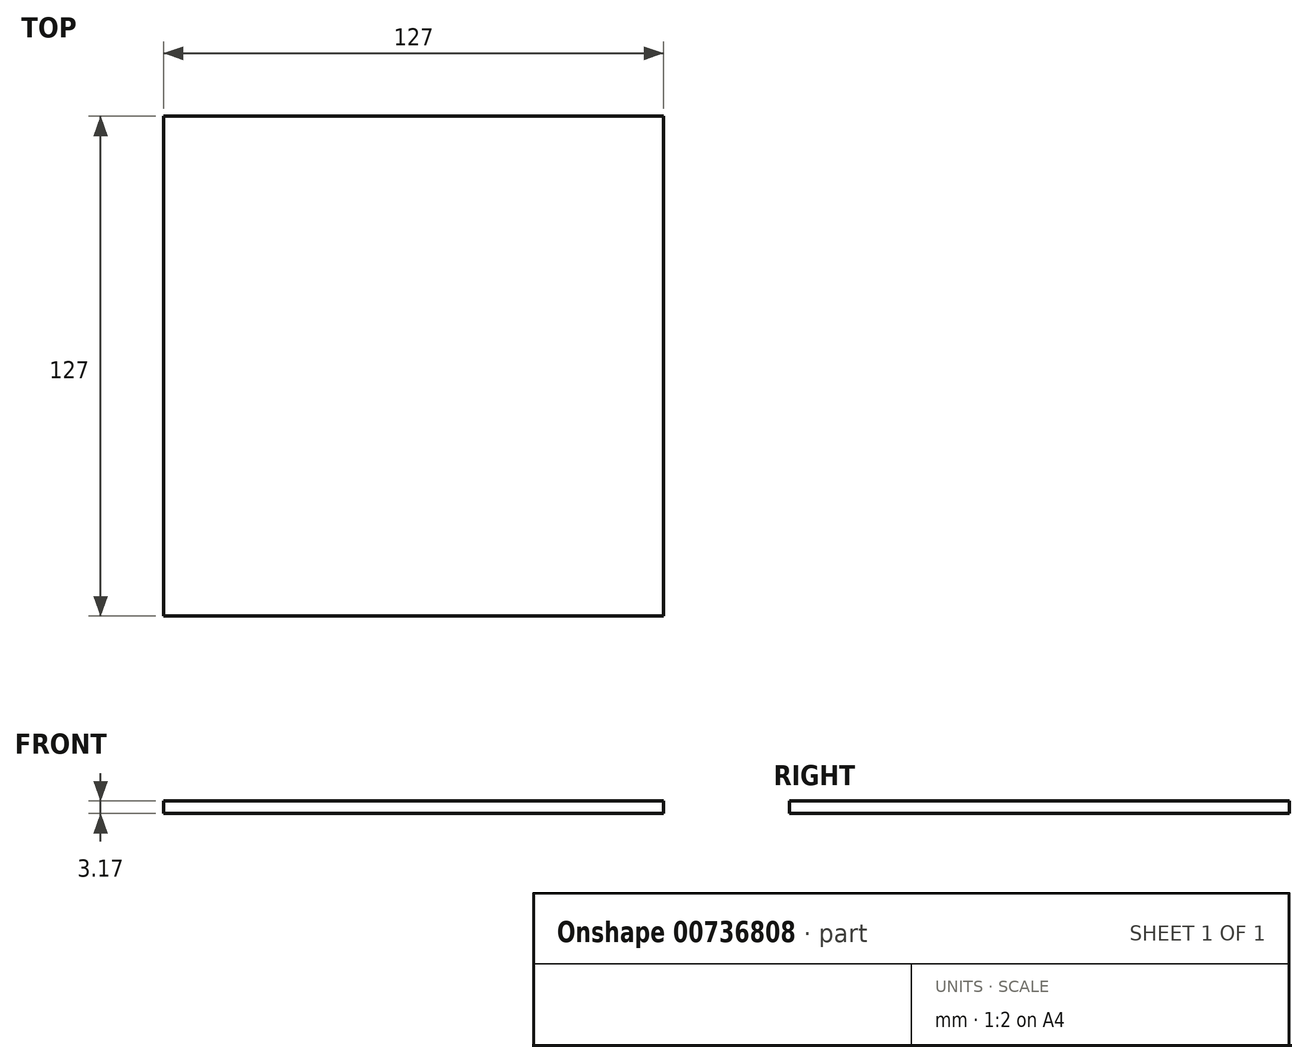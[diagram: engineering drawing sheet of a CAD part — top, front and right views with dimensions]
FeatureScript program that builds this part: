
annotation { "Feature Type Name" : "Feature", "Feature Type Description" : "" }
export const myFeature = defineFeature(function(context is Context, id is Id, definition is map)
    precondition{}
    {
        {
            var Q0;
            Q0=qCreatedBy(makeId("Top.planeOp"),FACE);
            var sketch = newSketch(context, id + "F0", { "sketchPlane" : qUnion([Q0])});
            skLineSegment(sketch, "E0.bottom", {"start": v(0, 0) * mm, "end": v(-127, 0) * mm});
            skLineSegment(sketch, "E0.top", {"start": v(0, 127) * mm, "end": v(-127, 127) * mm});
            skLineSegment(sketch, "E0.left", {"start": v(0, 0) * mm, "end": v(0, 127) * mm});
            skLineSegment(sketch, "E0.right", {"start": v(-127, 0) * mm, "end": v(-127, 127) * mm});
            skSolve(sketch);
        }
        {
            var Q0;
            Q0=makeQuery(id+"F0.imprint","IMPRINT",FACE,{"disambiguationData":[TD([[makeQuery(id+"F0.imprint","IMPRINT",EDGE,{"derivedFrom":sQuery(id+"F0.wireOp",EDGE,"E0.bottom")}),-1.0]])]});
            extrude(context, id + "F1", {"entities" : qUnion([Q0]), "depth" : 3.17 * mm, "offsetDistance" : 25.4 * mm});
        }
    });
